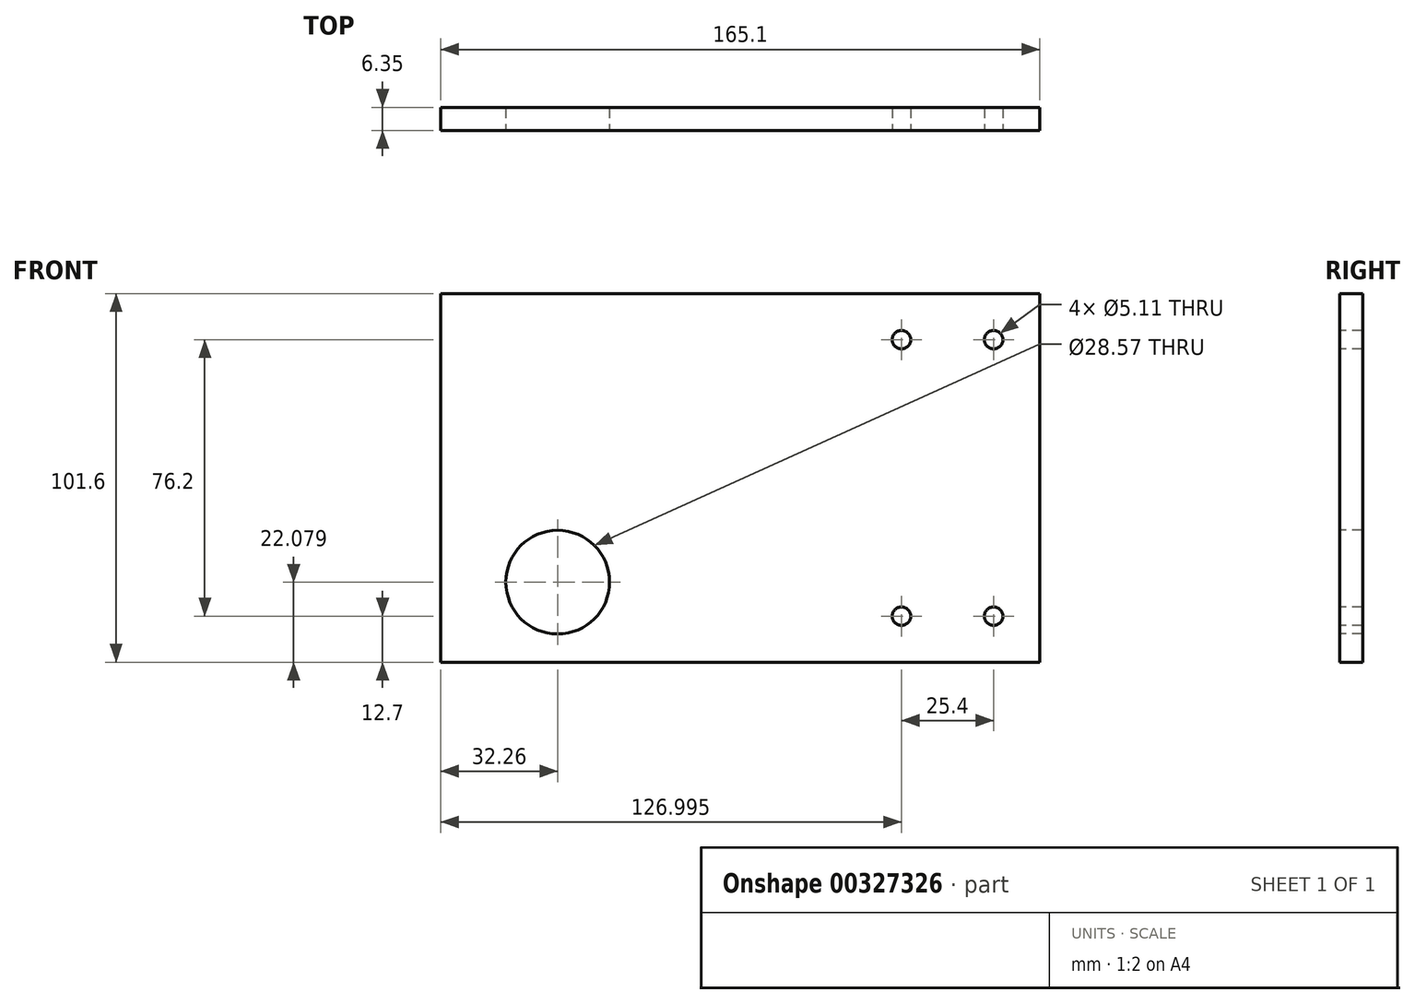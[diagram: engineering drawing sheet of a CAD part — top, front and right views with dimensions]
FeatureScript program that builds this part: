
annotation { "Feature Type Name" : "Feature", "Feature Type Description" : "" }
export const myFeature = defineFeature(function(context is Context, id is Id, definition is map)
    precondition{}
    {
        {
            var Q0;
            Q0=qCreatedBy(makeId("Front.planeOp"),FACE);
            var sketch = newSketch(context, id + "F0", { "sketchPlane" : qUnion([Q0])});
            skLineSegment(sketch, "E0.bottom", {"start": v(-234.12, 101.6) * mm, "end": v(-69.02, 101.6) * mm});
            skLineSegment(sketch, "E0.top", {"start": v(-234.12, 0) * mm, "end": v(-69.02, 0) * mm});
            skLineSegment(sketch, "E0.left", {"start": v(-234.12, 101.6) * mm, "end": v(-234.12, 0) * mm});
            skLineSegment(sketch, "E0.right", {"start": v(-69.02, 101.6) * mm, "end": v(-69.02, 0) * mm});
            skSolve(sketch);
        }
        {
            var Q0;
            Q0=makeQuery(id+"F0.imprint","IMPRINT",FACE,{"disambiguationData":[TD([[makeQuery(id+"F0.imprint","IMPRINT",EDGE,{"derivedFrom":sQuery(id+"F0.wireOp",EDGE,"E0.bottom")}),-1.0]])]});
            extrude(context, id + "F1", {"entities" : qUnion([Q0]), "depth" : 6.35 * mm});
        }
        {
            var Q0;
            Q0=makeQuery(id+"F1.opExtrude","CAP_FACE",FACE,{"disambiguationData":[OSD([sQuery(id+"F0.wireOp",EDGE,"E0.bottom"),sQuery(id+"F0.wireOp",EDGE,"E0.top"),sQuery(id+"F0.wireOp",EDGE,"E0.left"),sQuery(id+"F0.wireOp",EDGE,"E0.right")])],"isStart":false});
            var sketch = newSketch(context, id + "F2", { "sketchPlane" : qUnion([Q0])});
            skCircle(sketch, "E1", {"center": v(-81.72, 88.9) * mm, "radius": 2.55 * mm});
            skCircle(sketch, "E2", {"center": v(-107.12, 88.9) * mm, "radius": 2.55 * mm});
            skCircle(sketch, "E3", {"center": v(-81.72, 12.7) * mm, "radius": 2.55 * mm});
            skCircle(sketch, "E4", {"center": v(-107.12, 12.7) * mm, "radius": 2.55 * mm});
            skSolve(sketch);
        }
        {
            var Q0;
            Q0=makeQuery(id+"F2.imprint","IMPRINT",FACE,{"disambiguationData":[TD([[makeQuery(id+"F2.imprint","IMPRINT",EDGE,{"derivedFrom":sQuery(id+"F2.wireOp",EDGE,"E4")}),1.0]])]});
            var Q1;
            Q1=makeQuery(id+"F2.imprint","IMPRINT",FACE,{"disambiguationData":[TD([[makeQuery(id+"F2.imprint","IMPRINT",EDGE,{"derivedFrom":sQuery(id+"F2.wireOp",EDGE,"E3")}),1.0]])]});
            var Q2;
            Q2=makeQuery(id+"F2.imprint","IMPRINT",FACE,{"disambiguationData":[TD([[makeQuery(id+"F2.imprint","IMPRINT",EDGE,{"derivedFrom":sQuery(id+"F2.wireOp",EDGE,"E2")}),1.0]])]});
            var Q3;
            Q3=makeQuery(id+"F2.imprint","IMPRINT",FACE,{"disambiguationData":[TD([[makeQuery(id+"F2.imprint","IMPRINT",EDGE,{"derivedFrom":sQuery(id+"F2.wireOp",EDGE,"E1")}),1.0]])]});
            extrude(context, id + "F3", {"entities" : qUnion([Q0, Q1, Q2, Q3]), "operationType" : NewBodyOperationType.REMOVE, "oppositeDirection" : true, "depth" : 25.4 * mm});
        }
        {
            var Q0;
            Q0=makeQuery(id+"F1.opExtrude","CAP_FACE",FACE,{"disambiguationData":[OSD([sQuery(id+"F0.wireOp",EDGE,"E0.bottom"),sQuery(id+"F0.wireOp",EDGE,"E0.top"),sQuery(id+"F0.wireOp",EDGE,"E0.left"),sQuery(id+"F0.wireOp",EDGE,"E0.right")])],"isStart":false});
            var sketch = newSketch(context, id + "F4", { "sketchPlane" : qUnion([Q0])});
            skCircle(sketch, "E5", {"center": v(-201.86, 22.08) * mm, "radius": 14.29 * mm});
            skSolve(sketch);
        }
        {
            var Q0;
            Q0=makeQuery(id+"F4.imprint","IMPRINT",FACE,{"disambiguationData":[TD([[makeQuery(id+"F4.imprint","IMPRINT",EDGE,{"derivedFrom":sQuery(id+"F4.wireOp",EDGE,"E5")}),1.0]])]});
            extrude(context, id + "F5", {"entities" : qUnion([Q0]), "operationType" : NewBodyOperationType.REMOVE, "oppositeDirection" : true, "depth" : 25.4 * mm});
        }
    });
